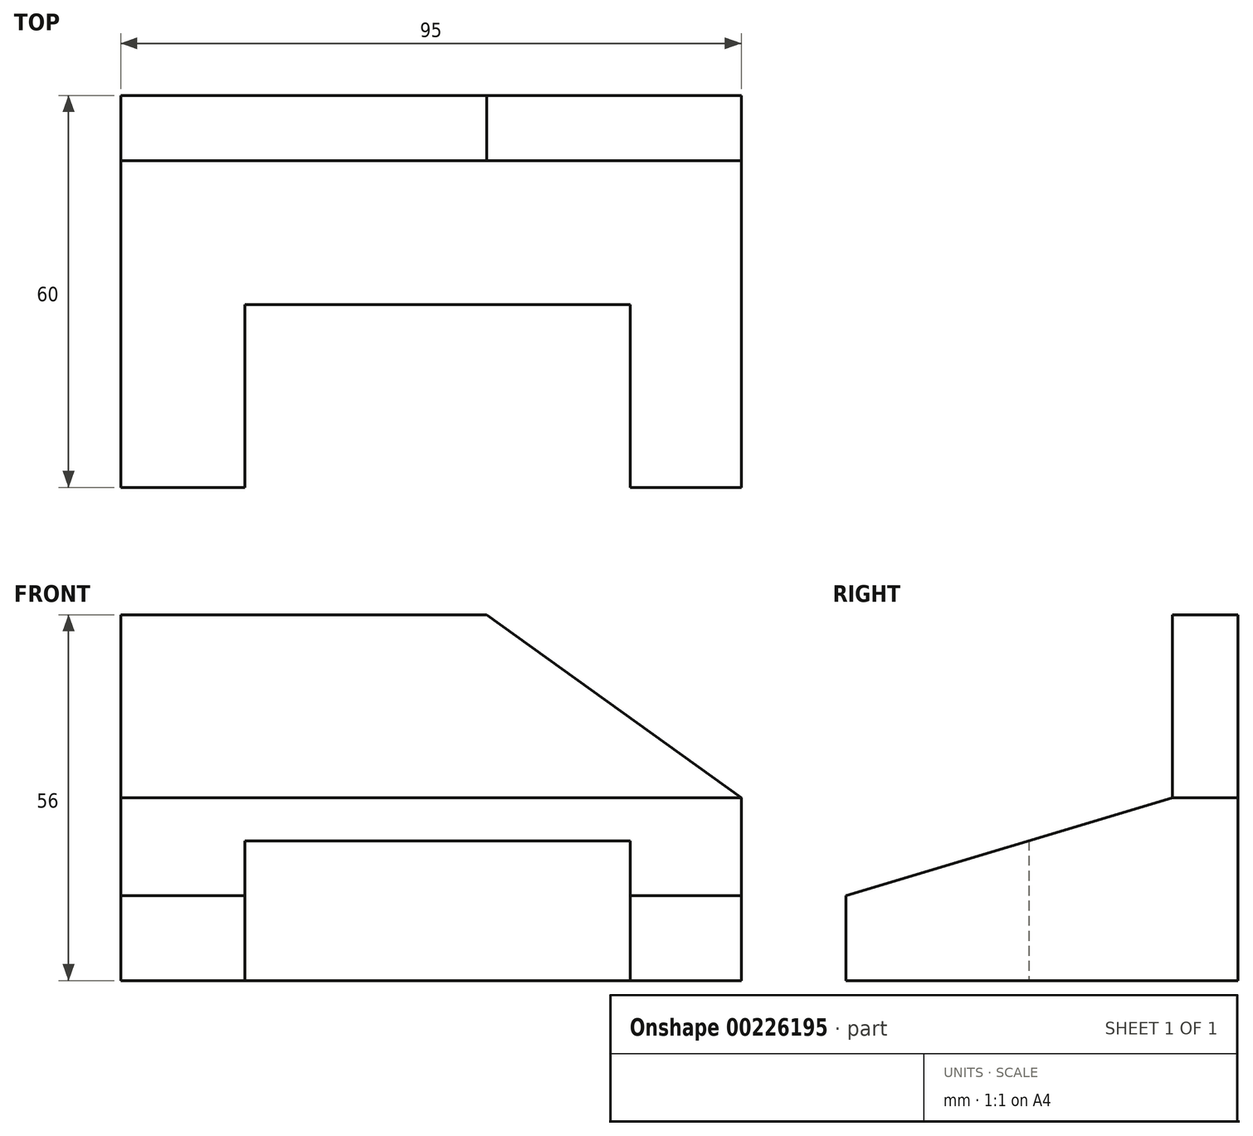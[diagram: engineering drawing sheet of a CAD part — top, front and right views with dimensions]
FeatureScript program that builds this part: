
annotation { "Feature Type Name" : "Feature", "Feature Type Description" : "" }
export const myFeature = defineFeature(function(context is Context, id is Id, definition is map)
    precondition{}
    {
        {
            var Q0;
            Q0=qCreatedBy(makeId("Right.planeOp"),FACE);
            var sketch = newSketch(context, id + "F0", { "sketchPlane" : qUnion([Q0])});
            skLineSegment(sketch, "E0", {"start": v(0, 0) * mm, "end": v(0, 56) * mm});
            skLineSegment(sketch, "E1", {"start": v(0, 56) * mm, "end": v(-10, 56) * mm});
            skLineSegment(sketch, "E2", {"start": v(-10, 56) * mm, "end": v(-10, 28) * mm});
            skLineSegment(sketch, "E3", {"start": v(-10, 28) * mm, "end": v(-60, 13) * mm});
            skLineSegment(sketch, "E4", {"start": v(-60, 13) * mm, "end": v(-60, 0) * mm});
            skLineSegment(sketch, "E5", {"start": v(-60, 0) * mm, "end": v(0, 0) * mm});
            skPoint(sketch, "E6", {"position": v(0, 28) * mm});
            skSolve(sketch);
        }
        {
            var Q0;
            Q0=makeQuery(id+"F0.imprint","IMPRINT",FACE,{"disambiguationData":[TD([[makeQuery(id+"F0.imprint","IMPRINT",EDGE,{"derivedFrom":sQuery(id+"F0.wireOp",EDGE,"E0")}),1.0]])]});
            extrude(context, id + "F1", {"entities" : qUnion([Q0]), "depth" : 95 * mm});
        }
        {
            var Q0;
            Q0=makeQuery(id+"F1.opExtrude","SWEPT_FACE",FACE,{"disambiguationData":[OSD([sQuery(id+"F0.wireOp",EDGE,"E2")])]});
            var sketch = newSketch(context, id + "F2", { "sketchPlane" : qUnion([Q0])});
            skLineSegment(sketch, "E7", {"start": v(56, 56) * mm, "end": v(95, 28) * mm});
            skSolve(sketch);
        }
        {
            var Q0;
            {var subQ0=sQuery(id+"F2.wireOp",EDGE,"E7");Q0=makeQuery(id+"F2.imprint","IMPRINT",FACE,{"disambiguationData":[TD([[makeQuery(id+"F2.imprint","IMPRINT",EDGE,{"derivedFrom":subQ0}),1.0]])]});}
            extrude(context, id + "F3", {"entities" : qUnion([Q0]), "operationType" : NewBodyOperationType.REMOVE, "endBound" : BoundingType.THROUGH_ALL, "oppositeDirection" : true, "depth" : 25 * mm});
        }
        {
            var Q0;
            Q0=makeQuery(id+"F1.opExtrude","SWEPT_FACE",FACE,{"disambiguationData":[OSD([sQuery(id+"F0.wireOp",EDGE,"E5")])]});
            var sketch = newSketch(context, id + "F4", { "sketchPlane" : qUnion([Q0])});
            skLineSegment(sketch, "E8.bottom", {"start": v(19, 60) * mm, "end": v(78, 60) * mm});
            skLineSegment(sketch, "E8.top", {"start": v(19, 32) * mm, "end": v(78, 32) * mm});
            skLineSegment(sketch, "E8.left", {"start": v(19, 60) * mm, "end": v(19, 32) * mm});
            skLineSegment(sketch, "E8.right", {"start": v(78, 60) * mm, "end": v(78, 32) * mm});
            skSolve(sketch);
        }
        {
            var Q0;
            Q0 = qSketchRegion(id + "F4", true);
            extrude(context, id + "F5", {"entities" : qUnion([Q0]), "operationType" : NewBodyOperationType.REMOVE, "oppositeDirection" : true, "depth" : 41.8 * mm});
        }
    });
